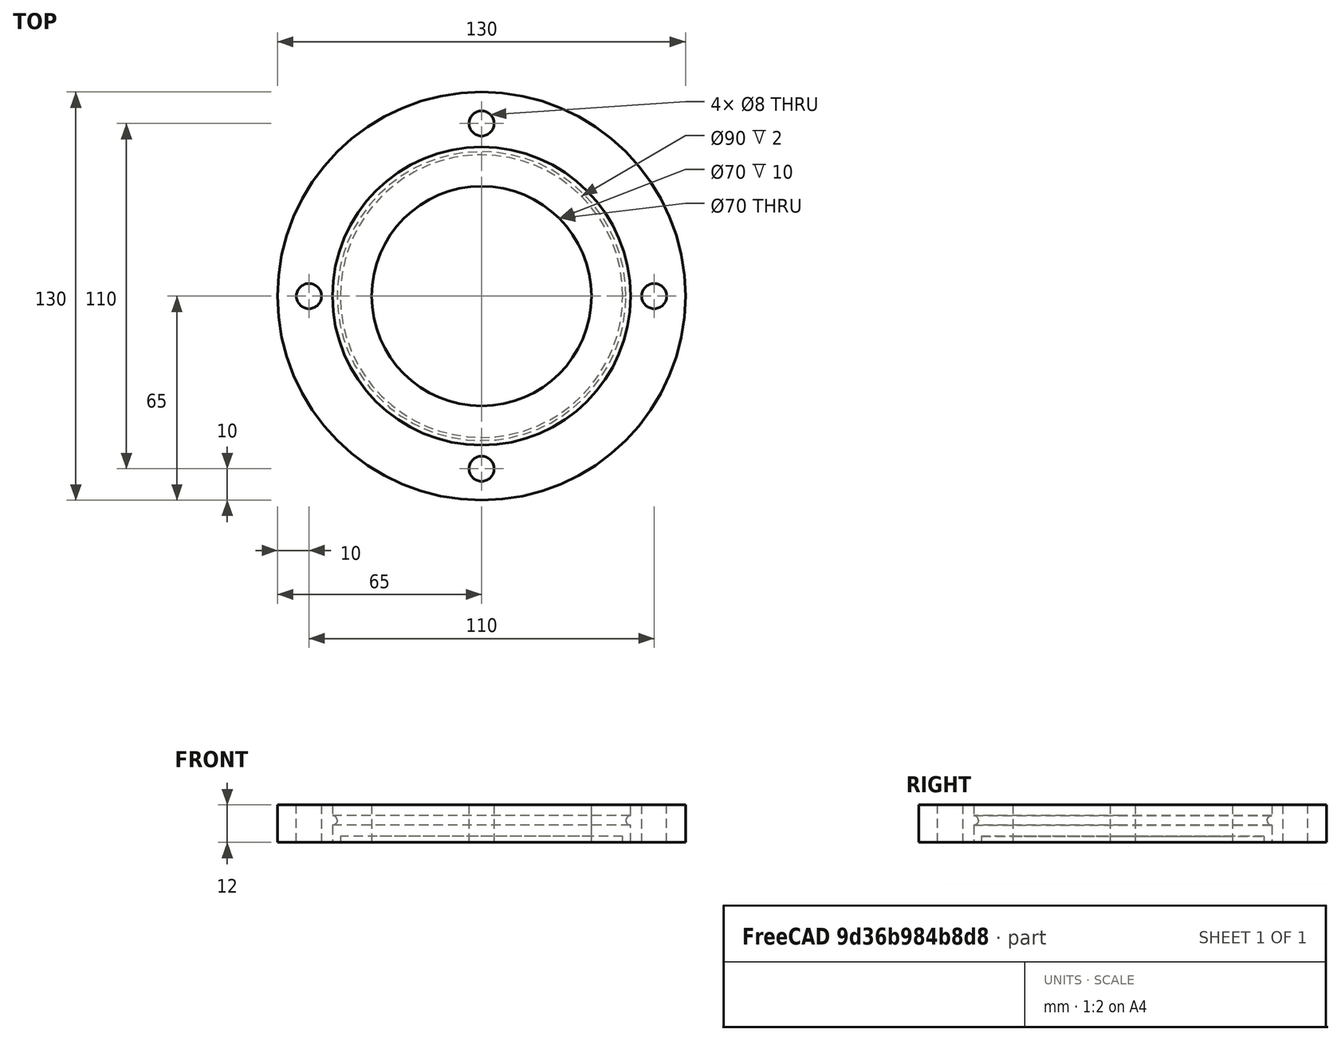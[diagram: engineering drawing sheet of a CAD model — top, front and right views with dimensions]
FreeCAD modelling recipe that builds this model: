
FCSTD DOCUMENT  (FreeCAD 1.0R1.0.0)
Label: IsoK
License: All rights reserved
LicenseURL: http://en.wikipedia.org/wiki/All_rights_reserved
objects: Part::Cylinder×6, Part::Cut×4, Spreadsheet::Sheet×1, Part::FeaturePython×1, Part::MultiFuse×1, Part::Torus×1
note: 12 computed .brp shape members not serialized (recipe doc carries the construction recipe); baked Part::Feature solids carry a one-line shape summary decoded from their .brp

FEATURE [Spreadsheet::Sheet] Spreadsheet  label="Iso1609"
  cells = A1='Nominal bore; B1='B; C1='C (H13); D1='x; E1='Bolt diameter; F1='Bolt count; G1='E; H1='F; I1='H; J1='M (js16); K1='L (js16); L1='P (h14); M1='r (b10); N1='S; O1='U; P1='V; A2==hiddenref(.nominal_bore.String); B2(dimB)==.B10; C2(dimC)==.C10; D2(dimx)==.D10; E2(boltdia)==.E10; F2(bolts)==.F10; G2(dimE)==.G10; H2(dimF)==.H10; I2(dimH)==.I10; J2(dimM)==.J10; K2(dimL)==.K10; L2(dimP)==.L10; M2(dimr)==.M10; N2(dimS)==.N10; O2(dimU)==.O10; P2(dimV)==.P10; A3='10; B3=40; C3=6.6; D3=0.6; E3=6; F3=4; G3=30; H3=12.2; I3=55; J3=8; K3=6; L3=3; M3=1; N3=30; O3=15; P3=28; A4='16; B4=45; C4=6.6; D4=0.6; E4=6; F4=4; G4=35; H4=17.2; I4=60; J4=8; K4=6; L4=3; M4=1; N4=35; O4=20; P4=33; A5='20; B5=50; C5=6.6; D5=0.6; E5=6; F5=4; G5=40; H5=22.2; I5=65; J5=8; K5=6; L5=3; M5=1; N5=40; O5=25; P5=38; A6='25; B6=55; C6=6.6; D6=0.6; E6=6; F6=4; G6=45; H6=26.2; I6=70; J6=8; K6=6; L6=3; M6=1; N6=45; O6=30; P6=43; A7='32; B7=70; C7=9; D7=1; E7=8; F7=4; G7=55; H7=34.2; I7=90; J7=8; K7=6; L7=3; M7=1; N7=55; O7=40; P7=53; A8='40; B8=80; C8=9; D8=1; E8=8; F8=4; G8=65; H8=41.2; I8=100; J8=12; K8=10; L8=5; M8=1.5; N8=65; O8=50; P8=62; A9='50; B9=90; C9=9; D9=1; E9=8; F9=4; G9=75; H9=52.2; I9=110; J9=12; K9=10; L9=5; M9=1.5; N9=75; O9=60; P9=72; A10='63; B10=110; C10=9; D10=1; E10=8; F10=4; G10=95; H10=70; I10=130; J10=12; K10=10; L10=5; M10=1.5; N10=95; O10=80; P10=92; A11='80; B11=125; C11=9; D11=1; E11=8; F11=8; G11=110; H11=83; I11=145; J11=12; K11=10; L11=5; M11=1.5; N11=110; O11=95; P11=107; A12='100; B12=145; C12=9; D12=1; E12=8; F12=8; G12=130; H12=102; I12=165; J12=12; K12=10; L12=5; M12=1.5; N12=130; O12=115; P12=127; A13='125; B13=175; C13=11; D13=1; E13=10; F13=8; G13=155; H13=127; +140 more cells
  nominal_bore = 7
  expr: .cells.Bind.B2.P2 = tuple(.cells; <<B>> + str(hiddenref(nominal_bore) + 3); <<P>> + str(hiddenref(nominal_bore) + 3))
  expr: .nominal_bore.Enum = cells[<<A3:|>>]
FEATURE [Part::Cylinder] Cylinder
  Angle = 360
  AttacherType = Attacher::AttachEngine3D
  FirstAngle = 0
  Height = 12
  Radius = 65
  SecondAngle = 0
  expr: Height = <<Iso1609>>.dimM
  expr: Radius = <<Iso1609>>.dimH / 2
FEATURE [Part::Cylinder] Cylinder001
  Angle = 360
  AttacherType = Attacher::AttachEngine3D
  FirstAngle = 0
  Height = 12
  Radius = 35
  SecondAngle = 0
  expr: Height = <<Iso1609>>.dimM
  expr: Radius = <<Iso1609>>.dimF / 2
FEATURE [Part::Cut] Cut  label="BoltedFlange_NotDrilled"
  Base = -> Cylinder
  Tool = -> Cylinder001
FEATURE [Part::Cylinder] Cylinder002
  Angle = 360
  AttacherType = Attacher::AttachEngine3D
  FirstAngle = 0
  Height = 12
  Placement = pos=(55,0,0) rot=(0,0,1;0rad)
  Radius = 4
  SecondAngle = 0
  expr: .Placement.Base.x = <<Iso1609>>.dimB / 2
  expr: Height = <<Iso1609>>.dimM
  expr: Radius = <<Iso1609>>.boltdia / 2
FEATURE [Part::FeaturePython] Array  # Draft array (typed FeaturePython)
  AlwaysSyncPlacement = false
  Angle = 360
  ArrayType = 1
  Axis = (0,0,1)
  Base = -> Cylinder002
  Center = (0,0,0)
  Count = 4
  ExpandArray = false
  Fuse = false
  IntervalAxis = (0,0,0)
  IntervalX = (50,0,0)
  IntervalY = (0,50,0)
  IntervalZ = (0,0,50)
  NumberCircles = 3
  NumberPolar = 4
  NumberX = 2
  NumberY = 2
  NumberZ = 1
  PlacementList = 4 placements: [(55,0,0),(1.22125e-14,55,0),(-55,6.73556e-15,0),(-1.22125e-14,-55,0)]
  RadialDistance = 50
  ScaleList = (4) [(1,1,1),(1,1,1),(1,1,1),(1,1,1)]
  Symmetry = 1
  TangentialDistance = 25
  expr: NumberPolar = <<Iso1609>>.bolts
FEATURE [Part::Cut] Cut001  label="BoltedFlange"
  Base = -> Cut
  Tool = -> Array
FEATURE [Part::Cylinder] Cylinder003
  Angle = 360
  AttacherType = Attacher::AttachEngine3D
  FirstAngle = 0
  Height = 12
  Radius = 47.5
  SecondAngle = 0
  expr: Height = <<Iso1609>>.dimL + 2
  expr: Radius = <<Iso1609>>.dimS / 2
FEATURE [Part::Cylinder] Cylinder004
  Angle = 360
  AttacherType = Attacher::AttachEngine3D
  FirstAngle = 0
  Height = 12
  Radius = 35
  SecondAngle = 0
  expr: Height = <<Iso1609>>.dimL + 2
  expr: Radius = <<Iso1609>>.dimF / 2
FEATURE [Part::Cylinder] Cylinder005
  Angle = 360
  AttacherType = Attacher::AttachEngine3D
  FirstAngle = 0
  Height = 2
  Radius = 45
  SecondAngle = 0
  expr: Radius = <<Iso1609>>.dimS / 2 - 2.5
FEATURE [Part::MultiFuse] Fusion
  Shapes = -> [Cylinder004,Cylinder005]
FEATURE [Part::Cut] Cut002
  Base = -> Cylinder003
  Tool = -> Fusion
FEATURE [Part::Torus] Torus
  Angle1 = -180
  Angle2 = 180
  Angle3 = 360
  AttacherType = Attacher::AttachEngine3D
  Placement = pos=(0,0,7) rot=(0,0,1;0rad)
  Radius1 = 47.5
  Radius2 = 1.5
  expr: .Placement.Base.z = <<Iso1609>>.dimL / 2 + 2
  expr: Radius1 = <<Iso1609>>.dimS / 2
  expr: Radius2 = <<Iso1609>>.dimr
FEATURE [Part::Cut] Cut003  label="CollarForClampedOrRotational"
  Base = -> Cut002
  Tool = -> Torus
